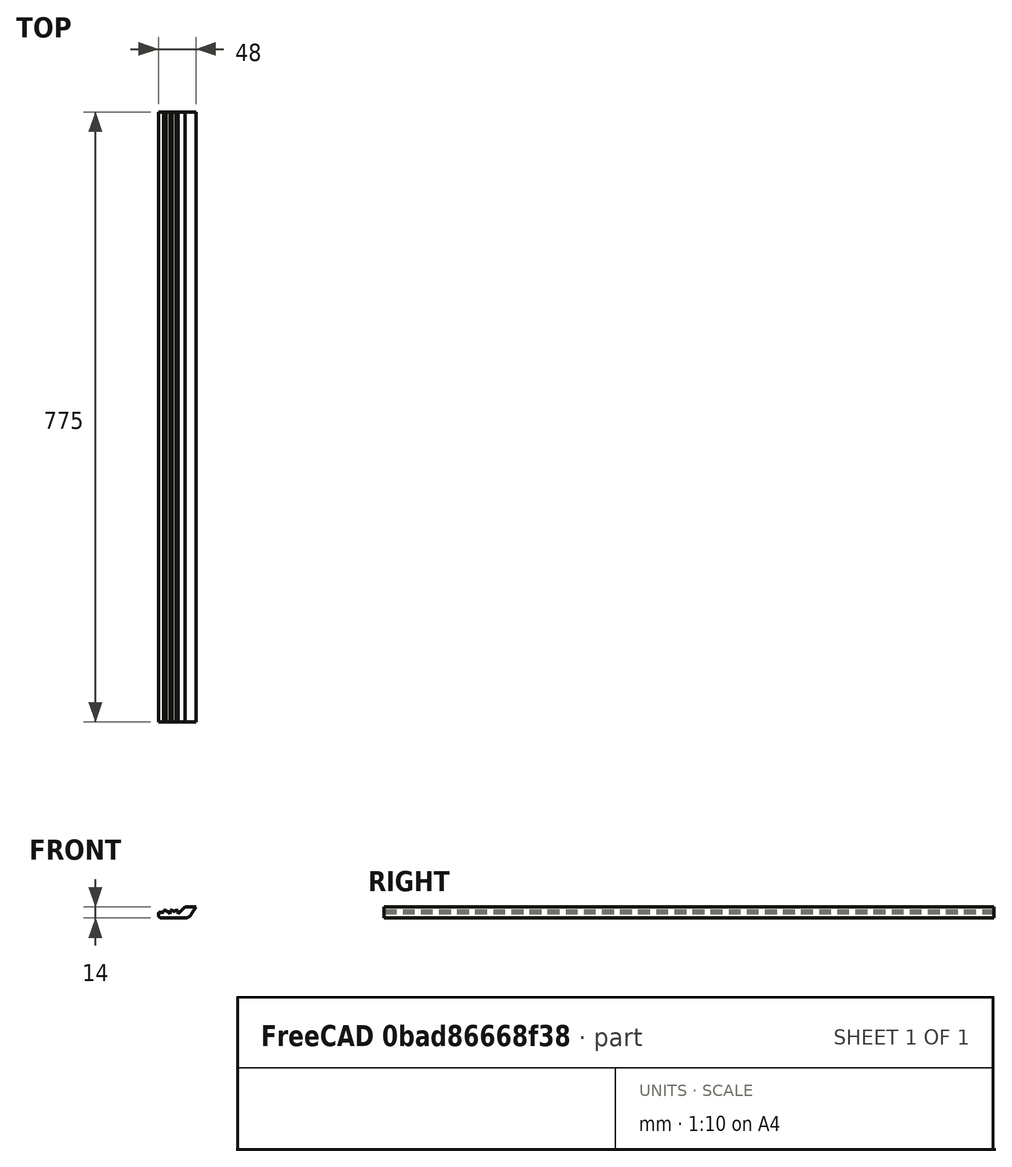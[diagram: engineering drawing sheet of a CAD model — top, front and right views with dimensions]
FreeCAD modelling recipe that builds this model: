
FCSTD DOCUMENT  (FreeCAD 0.20R)
Label: decor
License: All rights reserved
LicenseURL: http://en.wikipedia.org/wiki/All_rights_reserved
objects: TechDraw::DrawViewDimension×26, TechDraw::DrawViewPart×5, TechDraw::DrawSVGTemplate×3, TechDraw::DrawViewAnnotation×3, TechDraw::DrawPage×3, Sketcher::SketchObject×2, TechDraw::DrawViewSymbol×2, PartDesign::Pad×1, PartDesign::Pocket×1, PartDesign::Body×1, App::FeaturePython×1
note: 7 computed .brp shape members not serialized (recipe doc carries the construction recipe); baked Part::Feature solids carry a one-line shape summary decoded from their .brp

FEATURE [Sketcher::SketchObject] Sketch
  FullyConstrained = true
  MapMode = 5
  Placement = pos=(0,0,0) rot=(1,0,0;1.5708rad)
  Support = -> [XZ_Plane]
  sketch-geometry (14):
    g0: LineSegment StartX=14 StartY=-4 StartZ=0 EndX=-16 EndY=-4 EndZ=0
    g1: LineSegment StartX=28 StartY=10 StartZ=0 EndX=14 EndY=10 EndZ=0
    g2: LineSegment StartX=14 StartY=10 StartZ=0 EndX=5 EndY=1 EndZ=0
    g3: LineSegment StartX=5 StartY=6 StartZ=0 EndX=-5 EndY=6 EndZ=0
    g4: LineSegment StartX=-5 StartY=6 StartZ=0 EndX=-5 EndY=1 EndZ=0
    g5: LineSegment StartX=-10 StartY=5.5 StartZ=0 EndX=-5 EndY=1 EndZ=0
    g6: LineSegment StartX=-10 StartY=5.5 StartZ=0 EndX=-13 EndY=5.5 EndZ=0
    g7: LineSegment StartX=-13 StartY=5.5 StartZ=0 EndX=-13 EndY=3 EndZ=0
    g8: LineSegment StartX=-13 StartY=3 StartZ=0 EndX=-20 EndY=3 EndZ=0
    g9: LineSegment StartX=-20 StartY=3 StartZ=0 EndX=-20 EndY=4e-16 EndZ=0
    g10: ArcOfCircle CenterX=-16 CenterY=0 CenterZ=0 NormalX=0 NormalY=0 NormalZ=1 AngleXU=0 Radius=4 StartAngle=3.14159 EndAngle=4.71239
    g11: ArcOfCircle CenterX=13.6734 CenterY=5.66 CenterZ=0 NormalX=0 NormalY=0 NormalZ=1 AngleXU=0 Radius=9.66552 StartAngle=4.74618 EndAngle=5.7073
    g12: LineSegment StartX=5 StartY=6 StartZ=0 EndX=5 EndY=1 EndZ=0
    g13: LineSegment StartX=21.78 StartY=0.396373 StartZ=0 EndX=28 EndY=10 EndZ=0
  constraints (41):
    c: Horizontal(g1)
    c: DistanceX(g1,g1) = 14
    c: Coincident(g2,g1)
    c: DistanceX(g2,g1) = 23
    c: DistanceX(g3,g3) = 10
    c: DistanceX(g5,g3) = 5
    c: Coincident(g4,g3)
    c: Vertical(g4)
    c: Coincident(g5,g4)
    c: Coincident(g6,g5)
    c: Horizontal(g6)
    c: DistanceX(g6,g6) = 3
    c: Coincident(g7,g6)
    c: Vertical(g7)
    c: Coincident(g8,g7)
    c: Horizontal(g8)
    c: DistanceX(g8,g8) = 7
    c: Coincident(g9,g8)
    c: DistanceY(g7,g7) = 2.5
    c: Tangent(g9,g10) = -1.5708
    c: Tangent(g0,g10) = 1.5708
    c: DistanceY(g9,g9) = 3
    c: Horizontal(g0)
    c: Vertical(g9)
    c: PointOnObject(g10,g-1)
    c: Radius(g10) = 4
    c: DistanceX(g0,g0) = 30
    c: Coincident(g12,g3)
    c: Coincident(g12,g2)
    c: Vertical(g12)
    c: DistanceY(g12,g12) = 5
    c: DistanceY(g0,g1) = 14
    c: DistanceY(g4,g4) = 5
    c: Coincident(g11,g0)
    c: Coincident(g13,g1)
    c: Angle(g1,g13) = 0.996059
    c: Symmetric(g3,g3,g-2)
    c: DistanceY(g0,g4) = 5
    c: Coincident(g13,g11)
    c: DistanceX(g2,g11) = 16.78
    c: DistanceY(g0,g11) = 9.66
FEATURE [PartDesign::Pad] Pad
  Direction = (0,-1,-2e-16)
  Length = 775
  Length2 = 10
  Placement = pos=(0,0,0) rot=(1,0,0;1.5708rad)
  Profile = -> Sketch
  ReferenceAxis = -> Sketch [N_Axis]
  Type = 0
FEATURE [Sketcher::SketchObject] Sketch001
  FullyConstrained = true
  MapMode = 5
  Placement = pos=(0,-775,1.6e-15) rot=(1,0,0;1.5708rad)
  Support = -> [Pad]
  sketch-geometry (2):
    g0: ArcOfCircle CenterX=0 CenterY=7.57 CenterZ=0 NormalX=0 NormalY=0 NormalZ=1 AngleXU=0 Radius=2.9 StartAngle=3.66621 EndAngle=5.75857
    g1: LineSegment StartX=-2.51 StartY=6.11745 StartZ=0 EndX=2.51 EndY=6.11745 EndZ=0
  constraints (7):
    c: PointOnObject(g0,g-2)
    c: Radius(g0) = 2.9
    c: DistanceY(g-1,g0) = 7.57
    c: DistanceX(g0,g0) = 5.02
    c: Coincident(g1,g0)
    c: Coincident(g1,g0)
    c: Horizontal(g1)
FEATURE [PartDesign::Pocket] Pocket
  BaseFeature = -> Pad
  Direction = (0,1,2e-16)
  Length = 800
  Length2 = 5
  Placement = pos=(0,0,0) rot=(1,0,0;1.5708rad)
  Profile = -> Sketch001
  ReferenceAxis = -> Sketch001 [N_Axis]
  Type = 0
FEATURE [PartDesign::Body] Body
  Group = -> [Sketch,Pad,Sketch001,Pocket]
  Origin = -> Origin
  Tip = -> Pocket
FEATURE [TechDraw::DrawSVGTemplate] Template
  EditableTexts = Designed_by_Name=MD Harrington; Drawing_number=Drawing number 1; FC-Date=25-01-24; FC-SC=1:1; FC-SH=Sheet-1; FC-Title=Staircase Decor; Subtitle=Done For Prince George Ogbebor; Weight=Weight
  Height = 210
  Orientation = 1
  Width = 297
FEATURE [TechDraw::DrawViewPart] View  label="Left View"
  CoarseView = false
  Direction = (0,-1,0)
  Focus = 100
  HardHidden = false
  IsoCount = 0
  IsoHidden = false
  IsoVisible = false
  LockPosition = false
  Perspective = false
  Rotation = 0
  ScaleType = 0
  SeamHidden = false
  SeamVisible = true
  SmoothHidden = false
  SmoothVisible = true
  Source = -> [Body]
  X = 224.311
  XDirection = (1,0,0)
  Y = 162.957
FEATURE [TechDraw::DrawViewDimension] Dimension
  AngleOverride = false
  Arbitrary = false
  ArbitraryTolerances = false
  EqualTolerance = true
  ExtensionAngle = 0
  FormatSpec = %.2w
  FormatSpecOverTolerance = %+.2w
  FormatSpecUnderTolerance = %+.2w
  Inverted = false
  LineAngle = 0
  LockPosition = false
  MeasureType = 1
  OverTolerance = 0
  References2D = -> [View]
  Rotation = 0
  ScaleType = 0
  TheoreticalExact = false
  Type = 1
  UnderTolerance = 0
  X = -0.286459
  Y = 33.1999
FEATURE [TechDraw::DrawViewDimension] Dimension002
  AngleOverride = false
  Arbitrary = false
  ArbitraryTolerances = false
  EqualTolerance = true
  ExtensionAngle = 0
  FormatSpec = %.2w
  FormatSpecOverTolerance = %+.2w
  FormatSpecUnderTolerance = %+.2w
  Inverted = false
  LineAngle = 0
  LockPosition = false
  MeasureType = 1
  OverTolerance = 0
  References2D = -> [View]
  Rotation = 0
  ScaleType = 0
  TheoreticalExact = false
  Type = 1
  UnderTolerance = 0
  X = 38.9144
  Y = 25.1234
FEATURE [TechDraw::DrawViewDimension] Dimension003
  AngleOverride = false
  Arbitrary = false
  ArbitraryTolerances = false
  EqualTolerance = true
  ExtensionAngle = 0
  FormatSpec = %.2w
  FormatSpecOverTolerance = %+.2w
  FormatSpecUnderTolerance = %+.2w
  Inverted = false
  LineAngle = 0
  LockPosition = false
  MeasureType = 1
  OverTolerance = 0
  References2D = -> [View]
  Rotation = 0
  ScaleType = 0
  TheoreticalExact = false
  Type = 1
  UnderTolerance = 0
  X = 25.0294
  Y = -15.625
FEATURE [TechDraw::DrawViewDimension] Dimension004
  AngleOverride = false
  Arbitrary = false
  ArbitraryTolerances = false
  EqualTolerance = true
  ExtensionAngle = 0
  FormatSpec = %.2w
  FormatSpecOverTolerance = %+.2w
  FormatSpecUnderTolerance = %+.2w
  Inverted = false
  LineAngle = 0
  LockPosition = false
  MeasureType = 1
  OverTolerance = 0
  References2D = -> [View]
  Rotation = 0
  ScaleType = 0
  TheoreticalExact = false
  Type = 1
  UnderTolerance = 0
  X = -36.5097
  Y = -23.6372
FEATURE [TechDraw::DrawViewPart] View001  label="Left View -2"
  CoarseView = false
  Direction = (0,-1,0)
  Focus = 100
  HardHidden = false
  IsoCount = 0
  IsoHidden = false
  IsoVisible = false
  LockPosition = false
  Perspective = false
  Rotation = 0
  ScaleType = 0
  SeamHidden = false
  SeamVisible = true
  SmoothHidden = false
  SmoothVisible = true
  Source = -> [Body]
  X = 92.5867
  XDirection = (1,0,0)
  Y = 162.96
FEATURE [TechDraw::DrawViewDimension] Dimension009
  AngleOverride = false
  Arbitrary = false
  ArbitraryTolerances = false
  EqualTolerance = true
  ExtensionAngle = 0
  FormatSpec = %.2w
  FormatSpecOverTolerance = %+.2w
  FormatSpecUnderTolerance = %+.2w
  Inverted = false
  LineAngle = 0
  LockPosition = false
  MeasureType = 1
  OverTolerance = 0
  References2D = -> [View001]
  Rotation = 0
  ScaleType = 0
  TheoreticalExact = false
  Type = 2
  UnderTolerance = 0
  X = -13.778
  Y = -26.3193
FEATURE [TechDraw::DrawViewDimension] Dimension010
  AngleOverride = false
  Arbitrary = false
  ArbitraryTolerances = false
  EqualTolerance = true
  ExtensionAngle = 0
  FormatSpec = %.2w
  FormatSpecOverTolerance = %+.2w
  FormatSpecUnderTolerance = %+.2w
  Inverted = false
  LineAngle = 0
  LockPosition = false
  MeasureType = 1
  OverTolerance = 0
  References2D = -> [View001]
  Rotation = 0
  ScaleType = 0
  TheoreticalExact = false
  Type = 2
  UnderTolerance = 0
  X = -42.6508
  Y = 25.0363
FEATURE [TechDraw::DrawViewDimension] Dimension011
  AngleOverride = false
  Arbitrary = false
  ArbitraryTolerances = false
  EqualTolerance = true
  ExtensionAngle = 0
  FormatSpec = R%.2w
  FormatSpecOverTolerance = %+.2w
  FormatSpecUnderTolerance = %+.2w
  Inverted = false
  LineAngle = 0
  LockPosition = false
  MeasureType = 1
  OverTolerance = 0
  References2D = -> [View001]
  Rotation = 0
  ScaleType = 0
  TheoreticalExact = false
  Type = 4
  UnderTolerance = 0
  X = -4.24329
  Y = 29.4201
FEATURE [TechDraw::DrawViewDimension] Dimension012
  AngleOverride = false
  Arbitrary = false
  ArbitraryTolerances = false
  EqualTolerance = true
  ExtensionAngle = 0
  FormatSpec = R%.2w
  FormatSpecOverTolerance = %+.2w
  FormatSpecUnderTolerance = %+.2w
  Inverted = false
  LineAngle = 0
  LockPosition = false
  MeasureType = 1
  OverTolerance = 0
  References2D = -> [View001]
  Rotation = 0
  ScaleType = 0
  TheoreticalExact = false
  Type = 4
  UnderTolerance = 0
  X = 28.9958
  Y = -23.7624
FEATURE [TechDraw::DrawViewDimension] Dimension013
  AngleOverride = false
  Arbitrary = false
  ArbitraryTolerances = false
  EqualTolerance = true
  ExtensionAngle = 0
  FormatSpec = R%.2w
  FormatSpecOverTolerance = %+.2w
  FormatSpecUnderTolerance = %+.2w
  Inverted = false
  LineAngle = 0
  LockPosition = false
  MeasureType = 1
  OverTolerance = 0
  References2D = -> [View001]
  Rotation = 0
  ScaleType = 0
  TheoreticalExact = false
  Type = 4
  UnderTolerance = 0
  X = -41.8671
  Y = -16.8317
FEATURE [TechDraw::DrawViewDimension] Dimension014
  AngleOverride = false
  Arbitrary = false
  ArbitraryTolerances = false
  EqualTolerance = true
  ExtensionAngle = 0
  FormatSpec = %.2w
  FormatSpecOverTolerance = %+.2w
  FormatSpecUnderTolerance = %+.2w
  Inverted = false
  LineAngle = 0
  LockPosition = false
  MeasureType = 1
  OverTolerance = 0
  References2D = -> [View001]
  Rotation = 0
  ScaleType = 0
  TheoreticalExact = false
  Type = 0
  UnderTolerance = 0
  X = 56.8291
  Y = 9.95388
FEATURE [TechDraw::DrawViewDimension] Dimension015
  AngleOverride = false
  Arbitrary = false
  ArbitraryTolerances = false
  EqualTolerance = true
  ExtensionAngle = 0
  FormatSpec = %.2w
  FormatSpecOverTolerance = %+.2w
  FormatSpecUnderTolerance = %+.2w
  Inverted = false
  LineAngle = 0
  LockPosition = false
  MeasureType = 1
  OverTolerance = 0
  References2D = -> [View001]
  Rotation = 0
  ScaleType = 0
  TheoreticalExact = false
  Type = 2
  UnderTolerance = 0
  X = -52.9832
  Y = -4.06964
FEATURE [TechDraw::DrawViewPart] View002  label="Left View -3"
  CoarseView = false
  Direction = (0,-1,0)
  Focus = 100
  HardHidden = false
  IsoCount = 0
  IsoHidden = false
  IsoVisible = false
  LockPosition = false
  Perspective = false
  Rotation = 0
  ScaleType = 0
  SeamHidden = false
  SeamVisible = true
  SmoothHidden = false
  SmoothVisible = true
  Source = -> [Body]
  X = 92.59
  XDirection = (1,0,0)
  Y = 87.5968
FEATURE [TechDraw::DrawViewDimension] Dimension016
  AngleOverride = false
  Arbitrary = false
  ArbitraryTolerances = false
  EqualTolerance = true
  ExtensionAngle = 0
  FormatSpec = %.2w
  FormatSpecOverTolerance = %+.2w
  FormatSpecUnderTolerance = %+.2w
  Inverted = false
  LineAngle = 0
  LockPosition = false
  MeasureType = 1
  OverTolerance = 0
  References2D = -> [View002]
  Rotation = 0
  ScaleType = 0
  TheoreticalExact = false
  Type = 1
  UnderTolerance = 0
  X = -30.9108
  Y = 24.0411
FEATURE [TechDraw::DrawViewDimension] Dimension017
  AngleOverride = false
  Arbitrary = false
  ArbitraryTolerances = false
  EqualTolerance = true
  ExtensionAngle = 0
  FormatSpec = %.2w
  FormatSpecOverTolerance = %+.2w
  FormatSpecUnderTolerance = %+.2w
  Inverted = false
  LineAngle = 0
  LockPosition = false
  MeasureType = 1
  OverTolerance = 0
  References2D = -> [View002]
  Rotation = 0
  ScaleType = 0
  TheoreticalExact = false
  Type = 1
  UnderTolerance = 0
  X = -36.9067
  Y = 11.939
FEATURE [TechDraw::DrawViewDimension] Dimension018
  AngleOverride = false
  Arbitrary = false
  ArbitraryTolerances = false
  EqualTolerance = true
  ExtensionAngle = 0
  FormatSpec = %.2w
  FormatSpecOverTolerance = %+.2w
  FormatSpecUnderTolerance = %+.2w
  Inverted = false
  LineAngle = 0
  LockPosition = false
  MeasureType = 1
  OverTolerance = 0
  References2D = -> [View002]
  Rotation = 0
  ScaleType = 0
  TheoreticalExact = false
  Type = 1
  UnderTolerance = 0
  X = -40.1218
  Y = -22.4669
FEATURE [TechDraw::DrawViewDimension] Dimension019
  AngleOverride = false
  Arbitrary = false
  ArbitraryTolerances = false
  EqualTolerance = true
  ExtensionAngle = 0
  FormatSpec = %.2w
  FormatSpecOverTolerance = %+.2w
  FormatSpecUnderTolerance = %+.2w
  Inverted = false
  LineAngle = 0
  LockPosition = false
  MeasureType = 1
  OverTolerance = 0
  References2D = -> [View002]
  Rotation = 0
  ScaleType = 0
  TheoreticalExact = false
  Type = 1
  UnderTolerance = 0
  X = 32.0838
  Y = 28.5034
FEATURE [TechDraw::DrawViewDimension] Dimension020
  AngleOverride = false
  Arbitrary = false
  ArbitraryTolerances = false
  EqualTolerance = true
  ExtensionAngle = 0
  FormatSpec = %.2w
  FormatSpecOverTolerance = %+.2w
  FormatSpecUnderTolerance = %+.2w
  Inverted = false
  LineAngle = 0
  LockPosition = false
  MeasureType = 1
  OverTolerance = 0
  References2D = -> [View002]
  Rotation = 0
  ScaleType = 0
  TheoreticalExact = false
  Type = 1
  UnderTolerance = 0
  X = 44.1276
  Y = 19.1288
FEATURE [TechDraw::DrawViewDimension] Dimension021
  AngleOverride = false
  Arbitrary = false
  ArbitraryTolerances = false
  EqualTolerance = true
  ExtensionAngle = 0
  FormatSpec = %.2w
  FormatSpecOverTolerance = %+.2w
  FormatSpecUnderTolerance = %+.2w
  Inverted = false
  LineAngle = 0
  LockPosition = false
  MeasureType = 1
  OverTolerance = 0
  References2D = -> [View002]
  Rotation = 0
  ScaleType = 0
  TheoreticalExact = false
  Type = 1
  UnderTolerance = 0
  X = 28.3398
  Y = -30.7423
FEATURE [TechDraw::DrawViewAnnotation] Annotation
  Font = osifont
  LineSpace = 80
  LockPosition = false
  MaxWidth = -1
  Rotation = 0
  ScaleType = 0
  Text = All Measurements in mm  Scale 1:1  | Views are cross Sections
  TextSize = 5
  TextStyle = 0
  X = 185.09
  Y = 118.724
FEATURE [TechDraw::DrawViewPart] View003  label="Left View -4"
  CoarseView = false
  Direction = (0,-1,0)
  Focus = 100
  HardHidden = false
  IsoCount = 0
  IsoHidden = false
  IsoVisible = false
  LockPosition = false
  Perspective = false
  Rotation = 0
  ScaleType = 0
  SeamHidden = false
  SeamVisible = true
  SmoothHidden = false
  SmoothVisible = true
  Source = -> [Body]
  X = 224.31
  XDirection = (1,0,0)
  Y = 87.6
FEATURE [TechDraw::DrawViewDimension] Dimension022
  AngleOverride = false
  Arbitrary = false
  ArbitraryTolerances = false
  EqualTolerance = true
  ExtensionAngle = 0
  FormatSpec = %.2w
  FormatSpecOverTolerance = %+.2w
  FormatSpecUnderTolerance = %+.2w
  Inverted = false
  LineAngle = 0
  LockPosition = false
  MeasureType = 1
  OverTolerance = 0
  References2D = -> [View003]
  Rotation = 0
  ScaleType = 0
  TheoreticalExact = false
  Type = 0
  UnderTolerance = 0
  X = 10.2669
  Y = -21.9595
FEATURE [TechDraw::DrawViewDimension] Dimension023
  AngleOverride = false
  Arbitrary = false
  ArbitraryTolerances = false
  EqualTolerance = true
  ExtensionAngle = 0
  FormatSpec = %.2w
  FormatSpecOverTolerance = %+.2w
  FormatSpecUnderTolerance = %+.2w
  Inverted = false
  LineAngle = 0
  LockPosition = false
  MeasureType = 1
  OverTolerance = 0
  References2D = -> [View003]
  Rotation = 0
  ScaleType = 0
  TheoreticalExact = false
  Type = 0
  UnderTolerance = 0
  X = -46.3842
  Y = -2.2983
FEATURE [TechDraw::DrawViewDimension] Dimension024
  AngleOverride = false
  Arbitrary = false
  ArbitraryTolerances = false
  EqualTolerance = true
  ExtensionAngle = 0
  FormatSpec = %.2w
  FormatSpecOverTolerance = %+.2w
  FormatSpecUnderTolerance = %+.2w
  Inverted = false
  LineAngle = 0
  LockPosition = false
  MeasureType = 1
  OverTolerance = 0
  References2D = -> [View003]
  Rotation = 0
  ScaleType = 0
  TheoreticalExact = false
  Type = 2
  UnderTolerance = 0
  X = -37.1115
  Y = 6.28767
FEATURE [TechDraw::DrawViewDimension] Dimension025
  AngleOverride = false
  Arbitrary = false
  ArbitraryTolerances = false
  EqualTolerance = true
  ExtensionAngle = 0
  FormatSpec = %.2w
  FormatSpecOverTolerance = %+.2w
  FormatSpecUnderTolerance = %+.2w
  Inverted = false
  LineAngle = 0
  LockPosition = false
  MeasureType = 1
  OverTolerance = 0
  References2D = -> [View003]
  Rotation = 0
  ScaleType = 0
  TheoreticalExact = false
  Type = 1
  UnderTolerance = 0
  X = -1.5224
  Y = 16.3556
FEATURE [TechDraw::DrawSVGTemplate] Template001
  EditableTexts = Designed_by_Name=MD Harrington; Drawing_number=Drawing number-2; FC-Date=Date; FC-SC=1:1; FC-SH=Sheet-2; FC-Title=Staircase Decor; Subtitle=Done For Prince George Ogbebor; Weight=Weight
  Height = 210
  Orientation = 1
  Width = 297
FEATURE [TechDraw::DrawViewSymbol] ActiveView001
  LockPosition = false
  Rotation = 0
  ScaleType = 2
  Symbol = <blob: 9936 chars omitted>
  X = 152.032
  Y = 132.645
FEATURE [TechDraw::DrawViewAnnotation] Annotation001
  Font = osifont
  LineSpace = 80
  LockPosition = false
  MaxWidth = -1
  Rotation = 0
  ScaleType = 0
  Text = Length of this is 77.7 cm
  TextSize = 5
  TextStyle = 0
  X = 78.623
  Y = 51.0042
FEATURE [TechDraw::DrawPage] Page001
  KeepUpdated = true
  NextBalloonIndex = 1
  ProjectionType = 0
  Template = -> Template001
  Views = -> [ActiveView001,Annotation001]
FEATURE [TechDraw::DrawViewDimension] Dimension026
  AngleOverride = false
  Arbitrary = false
  ArbitraryTolerances = false
  EqualTolerance = true
  ExtensionAngle = 0
  FormatSpec = %.2w
  FormatSpecOverTolerance = %+.2w
  FormatSpecUnderTolerance = %+.2w
  Inverted = false
  LineAngle = 0
  LockPosition = false
  MeasureType = 1
  OverTolerance = 0
  References2D = -> [View003]
  Rotation = 0
  ScaleType = 0
  TheoreticalExact = false
  Type = 2
  UnderTolerance = 0
  X = 37.0618
  Y = 17.2752
FEATURE [TechDraw::DrawViewDimension] Dimension027
  AngleOverride = false
  Arbitrary = false
  ArbitraryTolerances = false
  EqualTolerance = true
  ExtensionAngle = 0
  FormatSpec = %.2w
  FormatSpecOverTolerance = %+.2w
  FormatSpecUnderTolerance = %+.2w
  Inverted = false
  LineAngle = 0
  LockPosition = false
  MeasureType = 1
  OverTolerance = 0
  References2D = -> [View002]
  Rotation = 0
  ScaleType = 0
  TheoreticalExact = false
  Type = 0
  UnderTolerance = 0
  X = 54.5713
  Y = 5.08893
FEATURE [TechDraw::DrawViewDimension] Dimension028
  AngleOverride = false
  Arbitrary = false
  ArbitraryTolerances = false
  EqualTolerance = true
  ExtensionAngle = 0
  FormatSpec = %.2w
  FormatSpecOverTolerance = %+.2w
  FormatSpecUnderTolerance = %+.2w
  Inverted = false
  LineAngle = 0
  LockPosition = false
  MeasureType = 1
  OverTolerance = 0
  References2D = -> [View002]
  Rotation = 0
  ScaleType = 0
  TheoreticalExact = false
  Type = 2
  UnderTolerance = 0
  X = -39.296
  Y = -1.52964
FEATURE [TechDraw::DrawPage] Page
  KeepUpdated = true
  NextBalloonIndex = 1
  ProjectionType = 0
  Template = -> Template
  Views = -> [View,Dimension,Dimension002,Dimension003,Dimension004,View001,Dimension009,Dimension010,Dimension011,Dimension012,Dimension013,Dimension014,Dimension015,View002,Dimension016,Dimension017,Dimension018,Dimension019,Dimension020,Dimension021,Annotation,View003,Dimension022,Dimension023,Dimension024,Dimension025,Dimension026,Dimension027,Dimension028]
FEATURE [TechDraw::DrawSVGTemplate] Template002
  EditableTexts = Designed_by_Name=MD Harrington; Drawing_number=Drawing number-3; FC-Date=25-01-2024; FC-SC=1:1; FC-SH=Sheet-4; FC-Title=Staircase Decor; Subtitle=Done For Prince George Ogbebor; Weight=Weight
  Height = 210
  Orientation = 1
  Width = 297
FEATURE [App::FeaturePython] Dimension029  # Draft dimension (typed FeaturePython)
  Diameter = false
  Dimline = (45.96,3.82,8.32)
  Direction = (0,0,0)
  Distance = 775
  End = (28,-775,10)
  LinkedGeometry = -> [Pocket]
  Normal = (-0.11,0.99,0.11)
  Start = (28,2.2e-15,10)
  Support = -> Pocket
FEATURE [TechDraw::DrawViewSymbol] ActiveView
  LockPosition = false
  Rotation = 0
  ScaleType = 2
  Symbol = <blob: 160521 chars omitted>
  X = 152.365
  Y = 141.505
FEATURE [TechDraw::DrawViewPart] View004
  CoarseView = false
  Direction = (0,1,0)
  Focus = 100
  HardHidden = false
  IsoCount = 0
  IsoHidden = false
  IsoVisible = false
  LockPosition = false
  Perspective = false
  Rotation = 0
  ScaleType = 0
  SeamHidden = false
  SeamVisible = true
  SmoothHidden = false
  SmoothVisible = true
  Source = -> [Body]
  X = 58.3881
  XDirection = (-1,0,0)
  Y = 84.8881
FEATURE [TechDraw::DrawViewDimension] Dimension030
  AngleOverride = false
  Arbitrary = false
  ArbitraryTolerances = false
  EqualTolerance = true
  ExtensionAngle = 0
  FormatSpec = %.2w
  FormatSpecOverTolerance = %+.2w
  FormatSpecUnderTolerance = %+.2w
  Inverted = false
  LineAngle = 0
  LockPosition = false
  MeasureType = 1
  OverTolerance = 0
  References2D = -> [View004]
  Rotation = 0
  ScaleType = 0
  TheoreticalExact = false
  Type = 6
  UnderTolerance = 0
  X = -7.57463
  Y = 18.5448
FEATURE [TechDraw::DrawViewDimension] Dimension031
  AngleOverride = false
  Arbitrary = false
  ArbitraryTolerances = false
  EqualTolerance = true
  ExtensionAngle = 0
  FormatSpec = %.2w
  FormatSpecOverTolerance = %+.2w
  FormatSpecUnderTolerance = %+.2w
  Inverted = false
  LineAngle = 0
  LockPosition = false
  MeasureType = 1
  OverTolerance = 0
  References2D = -> [View004]
  Rotation = 0
  ScaleType = 0
  TheoreticalExact = false
  Type = 6
  UnderTolerance = 0
  X = -30.5597
  Y = 12.7985
FEATURE [TechDraw::DrawViewAnnotation] Annotation002
  Font = osifont
  LineSpace = 80
  LockPosition = false
  MaxWidth = -1
  Rotation = 0
  ScaleType = 0
  Text = Shows 3D view and Angles of Decor | Scale is 1:1 save that of 3D Image 
  TextSize = 5
  TextStyle = 0
  X = 148.5
  Y = 105
FEATURE [TechDraw::DrawPage] Page002
  KeepUpdated = true
  NextBalloonIndex = 1
  ProjectionType = 0
  Template = -> Template002
  Views = -> [ActiveView,View004,Dimension030,Dimension031,Annotation002]
